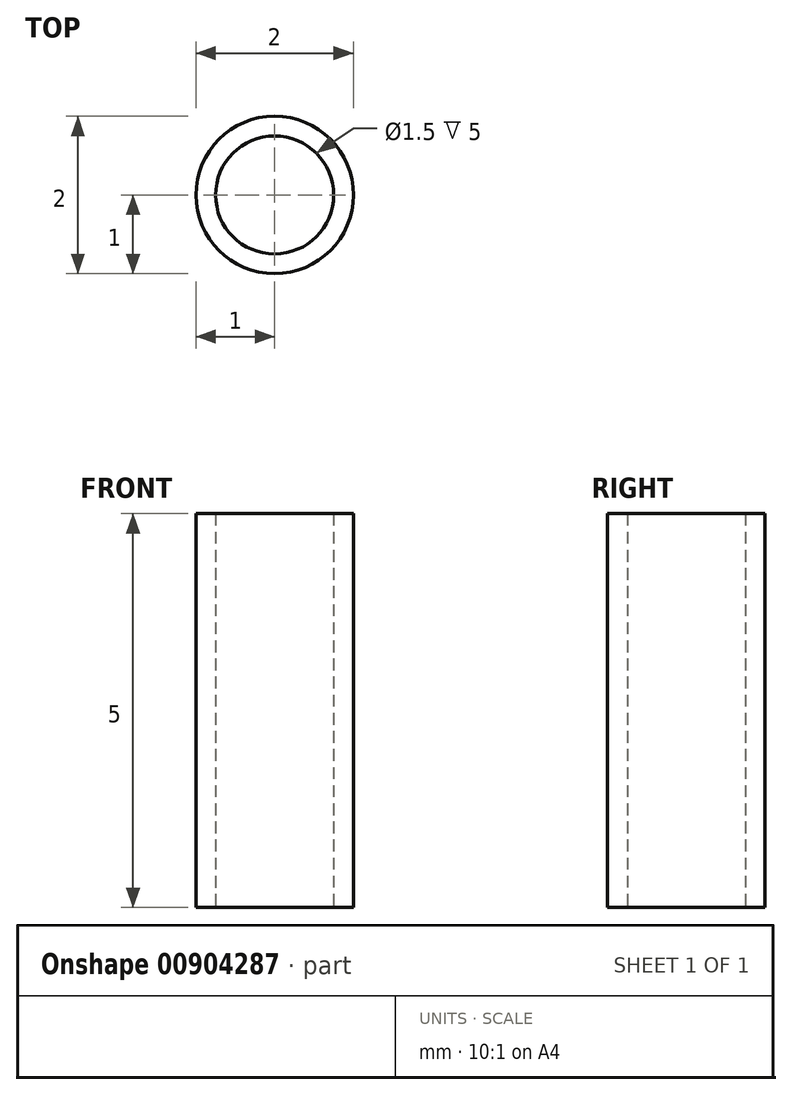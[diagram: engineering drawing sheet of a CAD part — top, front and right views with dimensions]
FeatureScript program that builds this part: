
annotation { "Feature Type Name" : "Feature", "Feature Type Description" : "" }
export const myFeature = defineFeature(function(context is Context, id is Id, definition is map)
    precondition{}
    {
        {
            var Q0;
            Q0=qCreatedBy(makeId("Front.planeOp"),FACE);
            var sketch = newSketch(context, id + "F0", { "sketchPlane" : qUnion([Q0])});
            skLineSegment(sketch, "E0.bottom", {"start": v(0, 0) * mm, "end": v(-0.75, 0) * mm});
            skLineSegment(sketch, "E0.top", {"start": v(0, 5) * mm, "end": v(-0.75, 5) * mm});
            skLineSegment(sketch, "E0.left", {"start": v(0, 0) * mm, "end": v(0, 5) * mm});
            skLineSegment(sketch, "E0.right", {"start": v(-0.75, 0) * mm, "end": v(-0.75, 5) * mm});
            skLineSegment(sketch, "E1.bottom", {"start": v(0, 0) * mm, "end": v(-1, 0) * mm});
            skLineSegment(sketch, "E1.top", {"start": v(0, 5) * mm, "end": v(-1, 5) * mm});
            skLineSegment(sketch, "E1.right", {"start": v(-1, 0) * mm, "end": v(-1, 5) * mm});
            skSolve(sketch);
        }
        {
            var Q0;
            {var subQ0=sQuery(id+"F0.wireOp",EDGE,"E0.right");Q0=makeQuery(id+"F0.imprint","IMPRINT",FACE,{"disambiguationData":[TD([[makeQuery(id+"F0.imprint","IMPRINT",EDGE,{"derivedFrom":subQ0}),1.0]])]});}
            var Q1;
            Q1=sQuery(id+"F0.wireOp",EDGE,"E0.left");
            revolve(context, id + "F1", {"surfaceOperationType" : NewSurfaceOperationType.NEW, "entities" : qUnion([Q0]), "axis" : qUnion([Q1]), "revolveType" : RevolveType.FULL});
        }
    });
